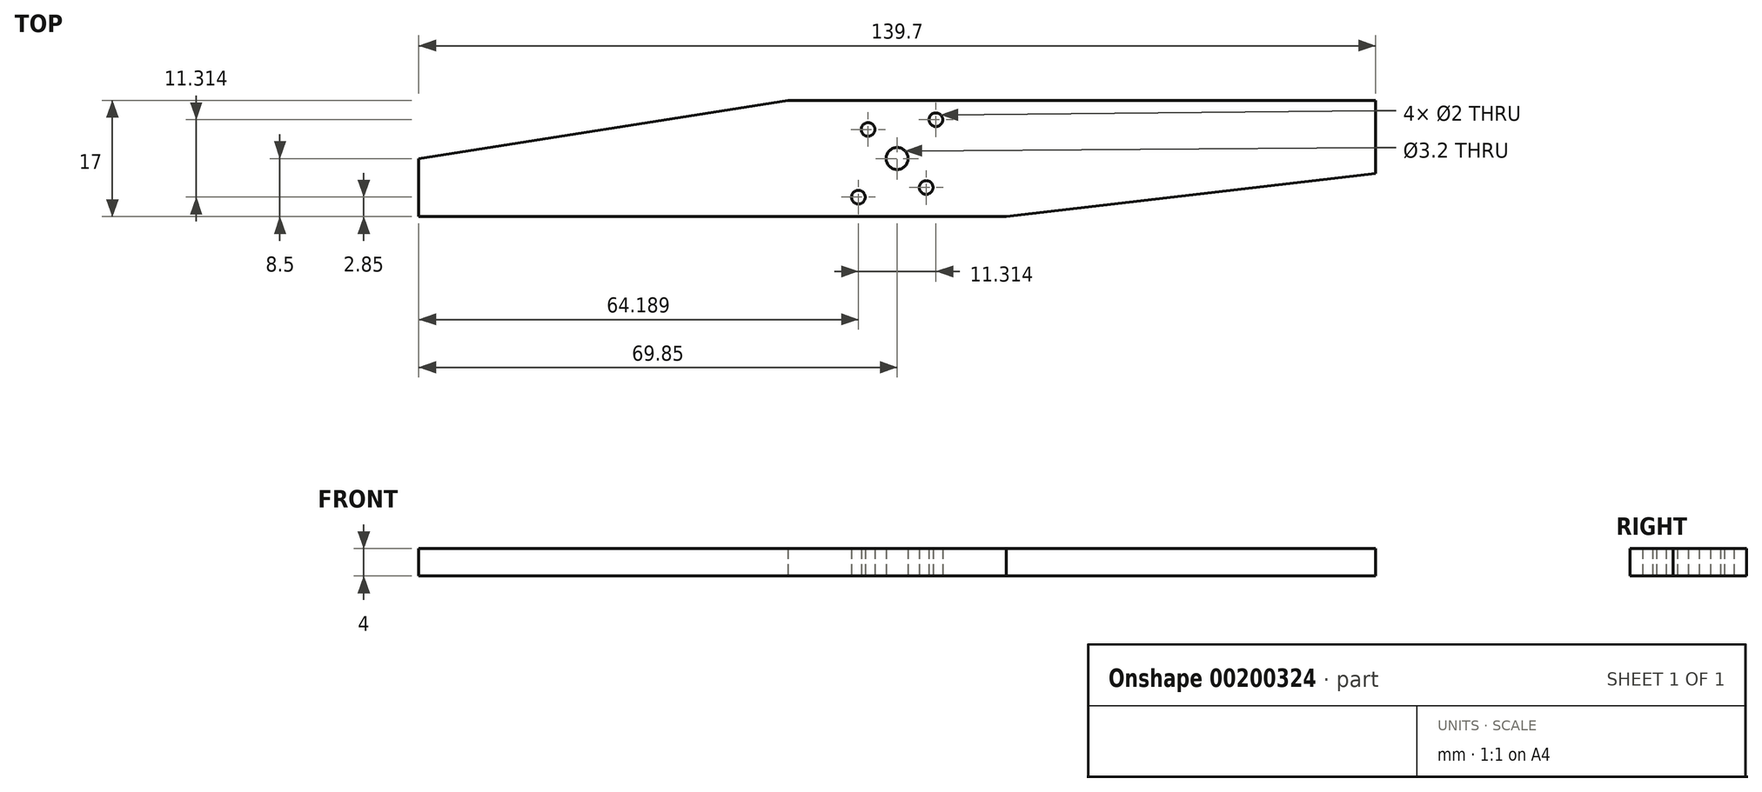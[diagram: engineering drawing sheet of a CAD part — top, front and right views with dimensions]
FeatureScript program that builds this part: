
annotation { "Feature Type Name" : "Feature", "Feature Type Description" : "" }
export const myFeature = defineFeature(function(context is Context, id is Id, definition is map)
    precondition{}
    {
        {
            var Q0;
            Q0=qCreatedBy(makeId("Top.planeOp"),FACE);
            var sketch = newSketch(context, id + "F0", { "sketchPlane" : qUnion([Q0])});
            skLineSegment(sketch, "E0", {"start": v(0, 37.01) * mm, "end": v(0, -48.21) * mm, "construction": true});
            skLineSegment(sketch, "E1.bottom", {"start": v(-69.85, -8.5) * mm, "end": v(69.85, -8.5) * mm});
            skLineSegment(sketch, "E1.top", {"start": v(-69.85, 8.5) * mm, "end": v(69.85, 8.5) * mm});
            skLineSegment(sketch, "E1.left", {"start": v(-69.85, -8.5) * mm, "end": v(-69.85, 8.5) * mm});
            skLineSegment(sketch, "E1.right", {"start": v(69.85, -8.5) * mm, "end": v(69.85, 8.5) * mm});
            skPoint(sketch, "E1.middle", {"position": v(0, 0) * mm});
            skCircle(sketch, "E2", {"center": v(0, 0) * mm, "radius": 1.6 * mm});
            skCircle(sketch, "E3", {"center": v(0, 0) * mm, "radius": 0.75 * mm});
            skCircle(sketch, "E4", {"center": v(-4.25, 4.25) * mm, "radius": 1 * mm});
            skCircle(sketch, "E5", {"center": v(5.65, 5.66) * mm, "radius": 1 * mm});
            skCircle(sketch, "E6", {"center": v(4.24, -4.24) * mm, "radius": 1 * mm});
            skCircle(sketch, "E7", {"center": v(-5.66, -5.65) * mm, "radius": 1 * mm});
            skLineSegment(sketch, "E8", {"start": v(-15.92, 8.5) * mm, "end": v(-69.85, 0) * mm});
            skLineSegment(sketch, "E9.MirrorCS", {"start": v(15.92, -8.5) * mm, "end": v(88.9, 0) * mm});
            skSolve(sketch);
        }
        {
            var Q0;
            Q0=makeQuery(id+"F0.imprint","IMPRINT",FACE,{"disambiguationData":[TD([[makeQuery(id+"F0.imprint","IMPRINT",EDGE,{"derivedFrom":sQuery(id+"F0.wireOp",EDGE,"FNoZNLft-ztMK-mgLG-BIdX-tsx6Lil6WcQ1.bottom")}),1.0]])]});
            var Q1;
            Q1=makeQuery(id+"F0.imprint","IMPRINT",FACE,{"disambiguationData":[TD([[makeQuery(id+"F0.imprint","IMPRINT",EDGE,{"derivedFrom":sQuery(id+"F0.wireOp",EDGE,"E2")}),-1.0]])]});
            extrude(context, id + "F1", {"entities" : qUnion([Q0, Q1]), "depth" : 4 * mm});
        }
    });
